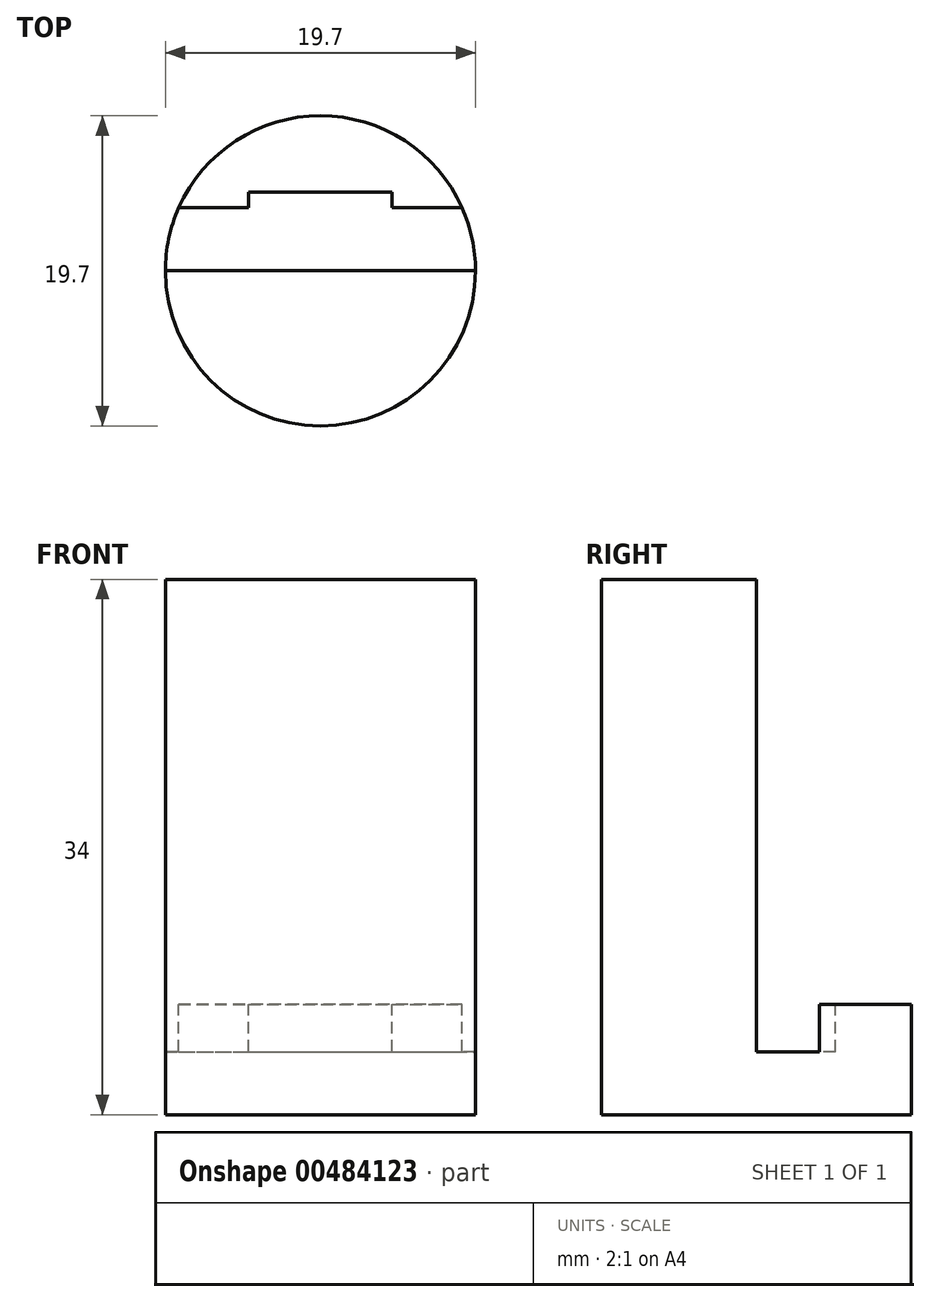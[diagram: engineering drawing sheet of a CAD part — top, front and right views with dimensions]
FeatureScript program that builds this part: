
annotation { "Feature Type Name" : "Feature", "Feature Type Description" : "" }
export const myFeature = defineFeature(function(context is Context, id is Id, definition is map)
    precondition{}
    {
        {
            var Q0;
            Q0=qCreatedBy(makeId("Top.planeOp"),FACE);
            var sketch = newSketch(context, id + "F0", { "sketchPlane" : qUnion([Q0])});
            skCircle(sketch, "E0", {"center": v(0, 0) * mm, "radius": 9.85 * mm});
            skSolve(sketch);
        }
        {
            var Q0;
            Q0=makeQuery(id+"F0.imprint","IMPRINT",FACE,{"disambiguationData":[TD([[makeQuery(id+"F0.imprint","IMPRINT",EDGE,{"derivedFrom":sQuery(id+"F0.wireOp",EDGE,"E0")}),1.0]])]});
            extrude(context, id + "F1", {"entities" : qUnion([Q0]), "depth" : 34 * mm});
        }
        {
            var Q0;
            Q0=makeQuery(id+"F1.opExtrude","CAP_FACE",FACE,{"disambiguationData":[OSD([sQuery(id+"F0.wireOp",EDGE,"E0")])],"isStart":false});
            var sketch = newSketch(context, id + "F2", { "sketchPlane" : qUnion([Q0])});
            skArc(sketch, "E1", {"start": v(9.85, 0) * mm, "mid": v(0, 9.85) * mm, "end": v(-9.85, 0) * mm});
            skLineSegment(sketch, "E2", {"start": v(-9.85, 0) * mm, "end": v(9.85, 0) * mm});
            skSolve(sketch);
        }
        {
            var Q0;
            Q0=makeQuery(id+"F2.imprint","IMPRINT",FACE,{"disambiguationData":[TD([[makeQuery(id+"F2.imprint","IMPRINT",EDGE,{"derivedFrom":sQuery(id+"F2.wireOp",EDGE,"E1")}),1.0]])]});
            extrude(context, id + "F3", {"entities" : qUnion([Q0]), "operationType" : NewBodyOperationType.REMOVE, "oppositeDirection" : true, "depth" : 27 * mm});
        }
        {
            var Q0;
            Q0=makeQuery(id+"F3.boolean.opBoolean","COPY",FACE,{"derivedFrom":makeQuery(id+"F3.opExtrude","CAP_FACE",FACE,{"disambiguationData":[OSD([sQuery(id+"F2.wireOp",EDGE,"E1"),sQuery(id+"F2.wireOp",EDGE,"E2")])],"isStart":false})});
            var sketch = newSketch(context, id + "F4", { "sketchPlane" : qUnion([Q0])});
            skLineSegment(sketch, "E3", {"start": v(-9.85, 0) * mm, "end": v(-9.85, 4) * mm});
            skLineSegment(sketch, "E4", {"start": v(-9.85, 4) * mm, "end": v(-4.55, 4) * mm});
            skLineSegment(sketch, "E5", {"start": v(-4.55, 4) * mm, "end": v(-4.55, 5) * mm});
            skLineSegment(sketch, "E6", {"start": v(-4.55, 5) * mm, "end": v(4.55, 5) * mm});
            skLineSegment(sketch, "E7", {"start": v(4.55, 5) * mm, "end": v(4.55, 4) * mm});
            skLineSegment(sketch, "E8", {"start": v(4.55, 4) * mm, "end": v(9.85, 4) * mm});
            skLineSegment(sketch, "E9", {"start": v(9.85, 4) * mm, "end": v(9.85, 0) * mm});
            skLineSegment(sketch, "E10", {"start": v(9.85, 0) * mm, "end": v(-9.85, 0) * mm});
            skSolve(sketch);
        }
        {
            var Q0;
            {var subQ1=sQuery(id+"F4.wireOp",EDGE,"E5");Q0=makeQuery(id+"F4.imprint","IMPRINT",FACE,{"disambiguationData":[TD([[makeQuery(id+"F4.imprint","IMPRINT",EDGE,{"derivedFrom":subQ1}),-1.0]])]});}
            extrude(context, id + "F5", {"entities" : qUnion([Q0]), "operationType" : NewBodyOperationType.REMOVE, "oppositeDirection" : true, "depth" : 3 * mm});
        }
    });
